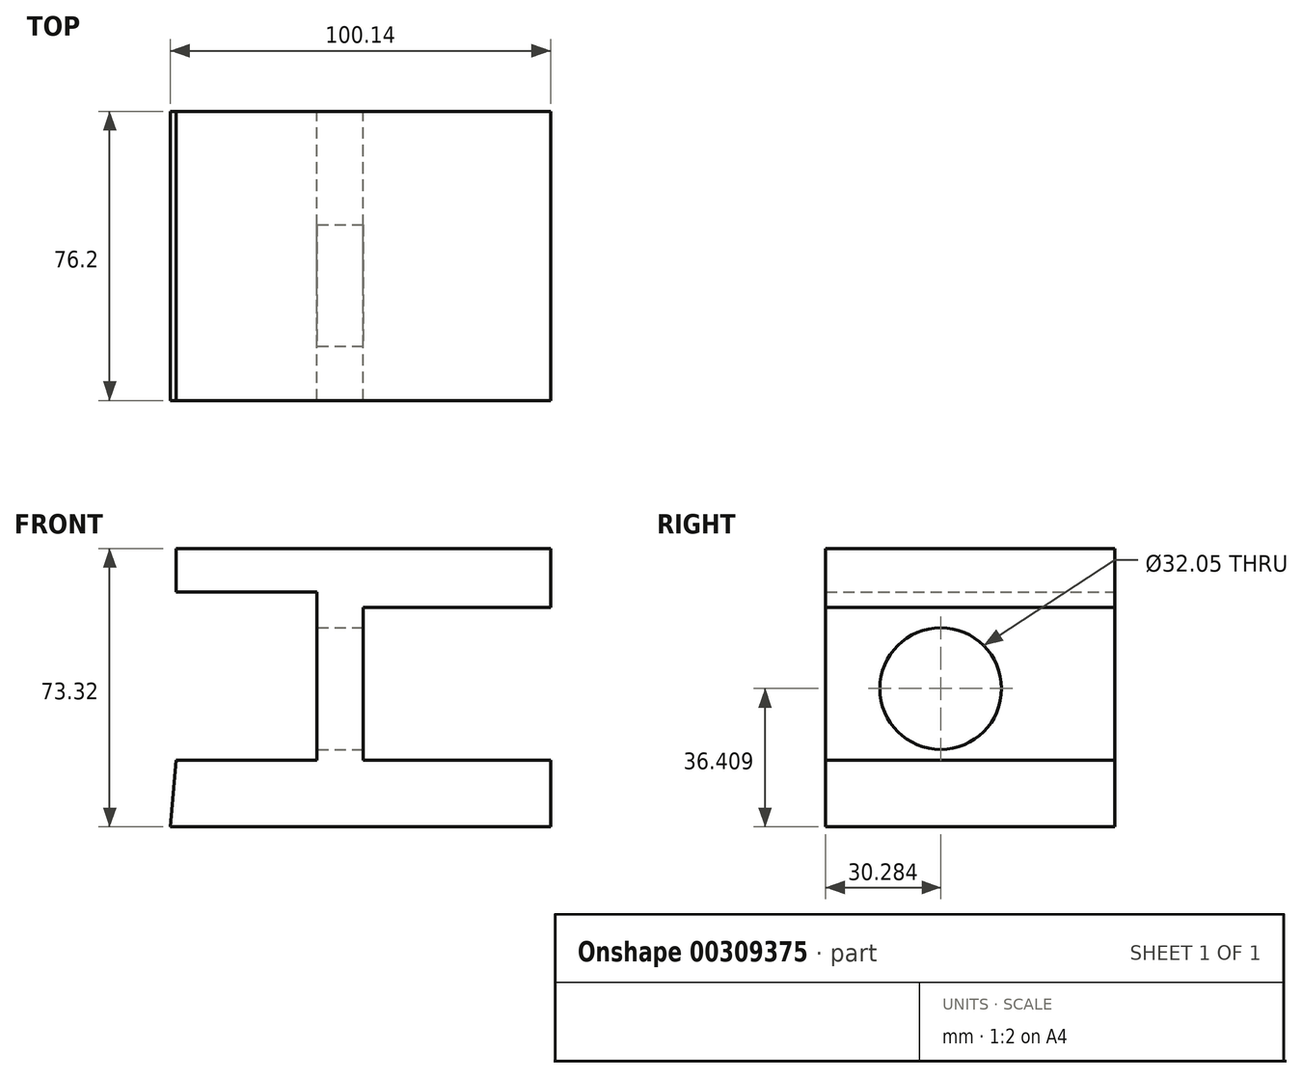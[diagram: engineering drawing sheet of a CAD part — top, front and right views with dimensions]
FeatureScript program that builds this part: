
annotation { "Feature Type Name" : "Feature", "Feature Type Description" : "" }
export const myFeature = defineFeature(function(context is Context, id is Id, definition is map)
    precondition{}
    {
        {
            var Q0;
            Q0=qCreatedBy(makeId("Front.planeOp"),FACE);
            var sketch = newSketch(context, id + "F0", { "sketchPlane" : qUnion([Q0])});
            skLineSegment(sketch, "E0", {"start": v(-44.85, -39.97) * mm, "end": v(55.3, -39.97) * mm});
            skLineSegment(sketch, "E1", {"start": v(55.3, -39.97) * mm, "end": v(55.3, -22.45) * mm});
            skLineSegment(sketch, "E2", {"start": v(55.3, -22.45) * mm, "end": v(5.94, -22.45) * mm});
            skLineSegment(sketch, "E3", {"start": v(5.94, -22.45) * mm, "end": v(5.94, 17.79) * mm});
            skLineSegment(sketch, "E4", {"start": v(5.94, 17.79) * mm, "end": v(55.3, 17.79) * mm});
            skLineSegment(sketch, "E5", {"start": v(55.3, 17.79) * mm, "end": v(55.3, 33.35) * mm});
            skLineSegment(sketch, "E6", {"start": v(55.3, 33.35) * mm, "end": v(-35.02, 33.35) * mm});
            skLineSegment(sketch, "E7", {"start": v(-35.02, 33.35) * mm, "end": v(-43.42, 33.35) * mm});
            skLineSegment(sketch, "E8", {"start": v(-43.42, 33.35) * mm, "end": v(-43.42, 21.9) * mm});
            skLineSegment(sketch, "E9", {"start": v(-43.42, 21.9) * mm, "end": v(-6.22, 21.9) * mm});
            skLineSegment(sketch, "E10", {"start": v(-6.22, 21.9) * mm, "end": v(-6.22, -22.45) * mm});
            skLineSegment(sketch, "E11", {"start": v(-6.22, -22.45) * mm, "end": v(-43.42, -22.45) * mm});
            skLineSegment(sketch, "E12", {"start": v(-43.42, -22.45) * mm, "end": v(-44.85, -39.97) * mm});
            skSolve(sketch);
        }
        {
            var Q0;
            Q0=makeQuery(id+"F0.imprint","IMPRINT",FACE,{"disambiguationData":[TD([[makeQuery(id+"F0.imprint","IMPRINT",EDGE,{"derivedFrom":sQuery(id+"F0.wireOp",EDGE,"E0")}),1.0]])]});
            extrude(context, id + "F1", {"entities" : qUnion([Q0]), "depth" : 76.2 * mm});
        }
        {
            var Q0;
            Q0=makeQuery(id+"F1.opExtrude","SWEPT_FACE",FACE,{"disambiguationData":[OSD([sQuery(id+"F0.wireOp",EDGE,"E3")])]});
            var sketch = newSketch(context, id + "F2", { "sketchPlane" : qUnion([Q0])});
            skCircle(sketch, "E13", {"center": v(-45.92, -3.56) * mm, "radius": 16.02 * mm});
            skSolve(sketch);
        }
        {
            var Q0;
            Q0=makeQuery(id+"F2.imprint","IMPRINT",FACE,{"disambiguationData":[TD([[makeQuery(id+"F2.imprint","IMPRINT",EDGE,{"derivedFrom":sQuery(id+"F2.wireOp",EDGE,"E13")}),1.0]])]});
            extrude(context, id + "F3", {"entities" : qUnion([Q0]), "operationType" : NewBodyOperationType.REMOVE, "oppositeDirection" : true, "depth" : 76.2 * mm});
        }
    });
